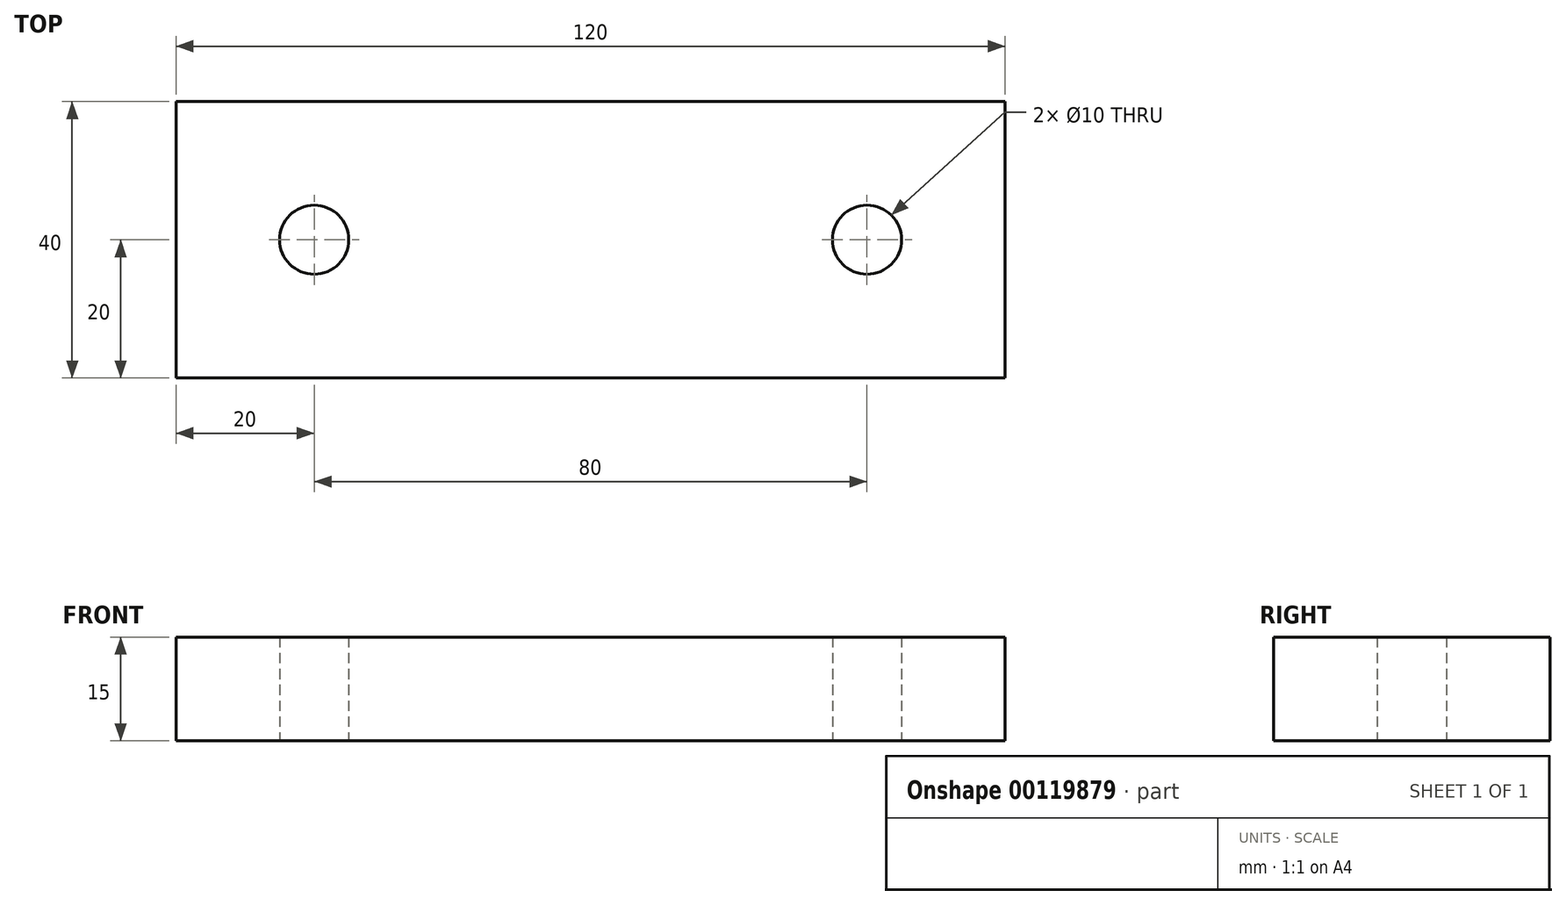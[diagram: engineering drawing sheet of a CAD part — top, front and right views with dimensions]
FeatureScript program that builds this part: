
annotation { "Feature Type Name" : "Feature", "Feature Type Description" : "" }
export const myFeature = defineFeature(function(context is Context, id is Id, definition is map)
    precondition{}
    {
        {
            var Q0;
            Q0=qCreatedBy(makeId("Top.planeOp"),FACE);
            var sketch = newSketch(context, id + "F0", { "sketchPlane" : qUnion([Q0])});
            skLineSegment(sketch, "E0.bottom", {"start": v(-60, -20) * mm, "end": v(60, -20) * mm});
            skLineSegment(sketch, "E0.top", {"start": v(-60, 20) * mm, "end": v(60, 20) * mm});
            skLineSegment(sketch, "E0.left", {"start": v(-60, -20) * mm, "end": v(-60, 20) * mm});
            skLineSegment(sketch, "E0.right", {"start": v(60, -20) * mm, "end": v(60, 20) * mm});
            skCircle(sketch, "E1", {"center": v(-40, 0) * mm, "radius": 5 * mm});
            skCircle(sketch, "E2", {"center": v(40, 0) * mm, "radius": 5 * mm});
            skSolve(sketch);
        }
        {
            var Q0;
            Q0=makeQuery(id+"F0.imprint","IMPRINT",FACE,{"disambiguationData":[TD([[makeQuery(id+"F0.imprint","IMPRINT",EDGE,{"derivedFrom":sQuery(id+"F0.wireOp",EDGE,"E0.bottom")}),1.0]])]});
            extrude(context, id + "F1", {"entities" : qUnion([Q0]), "depth" : 15 * mm});
        }
    });
